# Revit family: HVAC_HangingSystems_Walraven_BIS_RapidRail_Cantilever_Arm_(BUP1000)_WM2
name_source: partatom
category: Mechanical Equipment
revit_build: Autodesk Revit MEP 2016 (Build: 20150220_1215(x64)
units: mm (PartAtom-declared; Revit-internal decimal feet)

## family parameters
Always vertical = No
Cut with Voids When Loaded = No
OmniClass Number = 23.60.30.11.17
OmniClass Title = Pipework/Ductwork Mechanical Fasteners/Supports
Part Type = Normal
Room Calculation Point = No
Round Connector Dimension = Use Diameter
Shared = No
Work Plane-Based = Yes

## types (2) — shared parameters
BIMobject category = Hanging Systems
BIMobject category code = hvac-hanging-systems
BIMobject main category = HVAC
BIMobject main category code = hvac
Brand url = https://www.walraven.com
Date of publishing = 7/20/2018
Default Elevation = 1219 mm
Description = cantilever arm
Design country = Netherlands
IFC Classification = Mechanical Fastener
IfcDescription = cantilever arm
IfcExportAs = IfcMechanicalFastenerType
IfcExportType = USERDEFINED
Manufacturer = Walraven
Manufacturer country = Netherlands
Manufacturer name = Walraven
Material main = Steel
Model = BIS RapidRail Cantilever Arm (BUP1000) WM2
NLRS_C_code_SfB_tabel1 = 50
OmniClass Code = 23-27 43 13
OmniClass Description = Mechanical Pipe Supports
Product Guid = 8b781bb7-c863-4edf-86f6-d141afa09032
Product SKU = bis-rapidrail-cantilever-arm-bup1000-wm2
Product data url = https://bimobject.com
Product family = Rail Systems
Product group = Cantilever Arms and Sets
Product url = https://www.walraven.com
QR code = http://bimobject.com
RSen_C_code_ETIM = EC010933
RSen_C_code_ETIM_url = https://prod.etim-international.com
RSen_C_content_modification_date = 26-06-2018
RSen_C_content_releasedate = 22-02-2018
RSen_C_intended_use = hanging systems
RSen_C_level_of_development = LOD400
RSen_C_material = steel
RSen_C_material_colour = grey
RSen_C_material_finish = BIS UltraProtect® 1000
Technical description = https://library.walraven.com
URL = https://www.walraven.com
Weight Net (Kg) = 0
lookup_table_name = BIS RapidRail Cantilever Arm (BUP1000) WM2
region_index = 1
zero-valued in all types: Edition number, Nominal height, Nominal width

## per-type parameters (varying)
| type | RSen_S_net_weight | type_index |
| 200mm | 0.46 kg | 1 |
| 300mm | 0.56 kg | 2 |

## geometry (parser evidence)
native form markers: Blend x2, Sweep x5
no freeform markers — native parametric forms only
